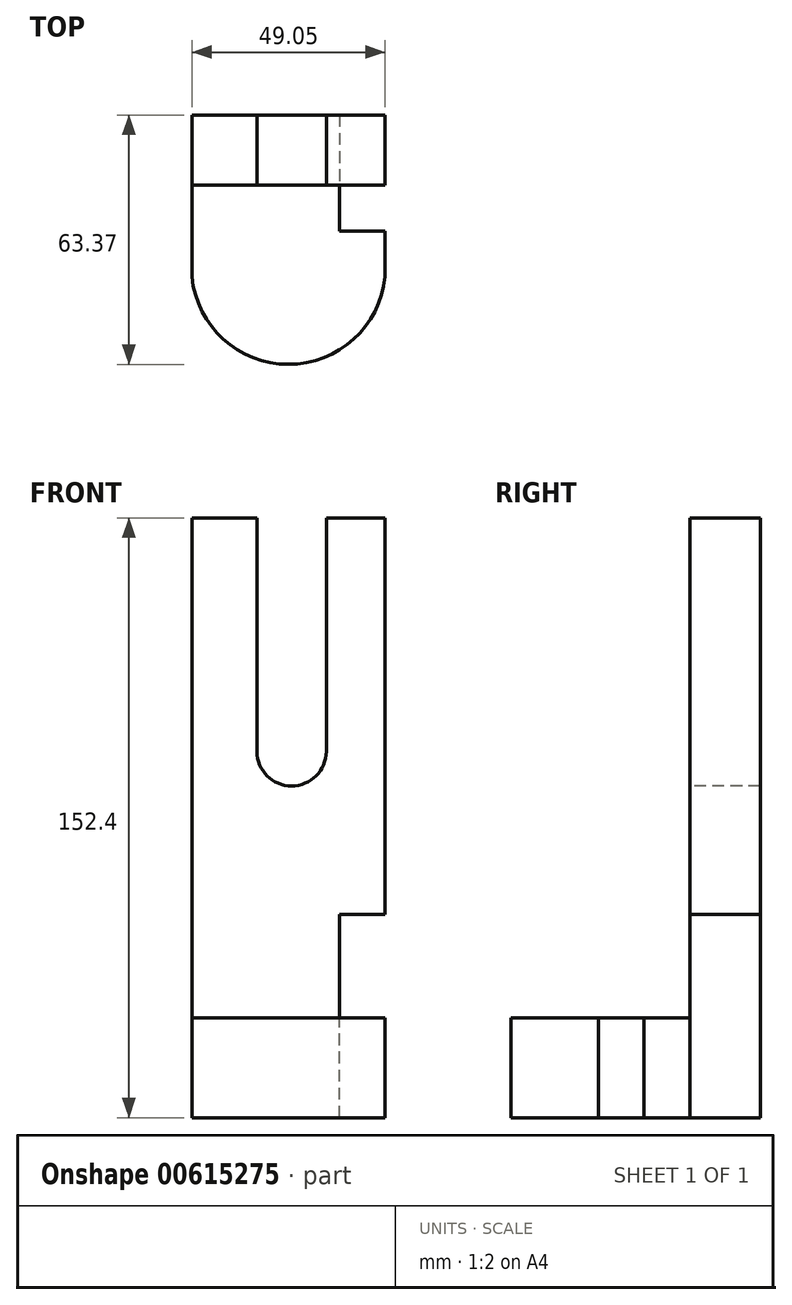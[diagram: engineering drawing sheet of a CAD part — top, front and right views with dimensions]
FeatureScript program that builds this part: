
annotation { "Feature Type Name" : "Feature", "Feature Type Description" : "" }
export const myFeature = defineFeature(function(context is Context, id is Id, definition is map)
    precondition{}
    {
        {
            var Q0;
            Q0=qCreatedBy(makeId("Top.planeOp"),FACE);
            var sketch = newSketch(context, id + "F0", { "sketchPlane" : qUnion([Q0])});
            skLineSegment(sketch, "E0.bottom", {"start": v(-76.32, -74.23) * mm, "end": v(-27.27, -74.23) * mm});
            skLineSegment(sketch, "E0.top", {"start": v(-76.32, -9.84) * mm, "end": v(-27.27, -9.84) * mm});
            skLineSegment(sketch, "E0.left", {"start": v(-76.32, -74.23) * mm, "end": v(-76.32, -9.84) * mm});
            skLineSegment(sketch, "E0.right", {"start": v(-27.27, -74.23) * mm, "end": v(-27.27, -9.84) * mm});
            skSolve(sketch);
        }
        {
            var Q0;
            Q0=makeQuery(id+"F0.imprint","IMPRINT",FACE,{"disambiguationData":[TD([[makeQuery(id+"F0.imprint","IMPRINT",EDGE,{"derivedFrom":sQuery(id+"F0.wireOp",EDGE,"E0.bottom")}),1.0]])]});
            extrude(context, id + "F1", {"entities" : qUnion([Q0]), "depth" : 25.4 * mm, "offsetDistance" : 25.4 * mm});
        }
        {
            var Q0;
            Q0=makeQuery(id+"F1.opExtrude","CAP_FACE",FACE,{"disambiguationData":[OSD([sQuery(id+"F0.wireOp",EDGE,"E0.bottom"),sQuery(id+"F0.wireOp",EDGE,"E0.top"),sQuery(id+"F0.wireOp",EDGE,"E0.left"),sQuery(id+"F0.wireOp",EDGE,"E0.right")])],"isStart":false});
            var sketch = newSketch(context, id + "F2", { "sketchPlane" : qUnion([Q0])});
            skLineSegment(sketch, "E1.bottom", {"start": v(-27.27, -9.84) * mm, "end": v(-76.32, -9.84) * mm});
            skLineSegment(sketch, "E1.top", {"start": v(-27.27, -27.72) * mm, "end": v(-76.32, -27.72) * mm});
            skLineSegment(sketch, "E1.left", {"start": v(-27.27, -9.84) * mm, "end": v(-27.27, -27.72) * mm});
            skLineSegment(sketch, "E1.right", {"start": v(-76.32, -9.84) * mm, "end": v(-76.32, -27.72) * mm});
            skSolve(sketch);
        }
        {
            var Q0;
            Q0=makeQuery(id+"F2.imprint","IMPRINT",FACE,{"disambiguationData":[TD([[makeQuery(id+"F2.imprint","IMPRINT",EDGE,{"derivedFrom":sQuery(id+"F2.wireOp",EDGE,"E1.bottom")}),-1.0]])]});
            extrude(context, id + "F3", {"entities" : qUnion([Q0]), "operationType" : NewBodyOperationType.ADD, "depth" : 127 * mm, "offsetDistance" : 25.4 * mm});
        }
        {
            var Q0;
            Q0=makeQuery(id+"F1.opExtrude","CAP_FACE",FACE,{"disambiguationData":[OSD([sQuery(id+"F0.wireOp",EDGE,"E0.bottom"),sQuery(id+"F0.wireOp",EDGE,"E0.top"),sQuery(id+"F0.wireOp",EDGE,"E0.left"),sQuery(id+"F0.wireOp",EDGE,"E0.right")])],"isStart":false});
            var sketch = newSketch(context, id + "F4", { "sketchPlane" : qUnion([Q0])});
            skArc(sketch, "E2", {"start": v(-76.32, -50.98) * mm, "mid": v(-51.8, -73.2) * mm, "end": v(-27.27, -50.98) * mm});
            skSolve(sketch);
        }
        {
            var Q0;
            {var subQ0=sQuery(id+"F4.wireOp",EDGE,"E2");Q0=makeQuery(id+"F4.imprint","IMPRINT",FACE,{"disambiguationData":[TD([[makeQuery(id+"F4.imprint","IMPRINT",EDGE,{"derivedFrom":subQ0}),-1.0]])]});}
            extrude(context, id + "F5", {"entities" : qUnion([Q0]), "operationType" : NewBodyOperationType.REMOVE, "oppositeDirection" : true, "depth" : 25.4 * mm, "offsetDistance" : 25.4 * mm});
        }
        {
            var Q0;
            Q0=makeQuery(id+"F1.opExtrude","CAP_FACE",FACE,{"disambiguationData":[OSD([sQuery(id+"F0.wireOp",EDGE,"E0.bottom"),sQuery(id+"F0.wireOp",EDGE,"E0.top"),sQuery(id+"F0.wireOp",EDGE,"E0.left"),sQuery(id+"F0.wireOp",EDGE,"E0.right")])],"isStart":false});
            var sketch = newSketch(context, id + "F6", { "sketchPlane" : qUnion([Q0])});
            skPoint(sketch, "E3.oppositeSnap0", {"position": v(-27.27, -39.35) * mm});
            skLineSegment(sketch, "E3.bottom", {"start": v(-27.27, -27.72) * mm, "end": v(-38.87, -27.72) * mm});
            skLineSegment(sketch, "E3.top", {"start": v(-27.27, -39.35) * mm, "end": v(-38.87, -39.35) * mm});
            skLineSegment(sketch, "E3.left", {"start": v(-27.27, -27.72) * mm, "end": v(-27.27, -39.35) * mm});
            skLineSegment(sketch, "E3.right", {"start": v(-38.87, -27.72) * mm, "end": v(-38.87, -39.35) * mm});
            skSolve(sketch);
        }
        {
            var Q0;
            Q0=makeQuery(id+"F6.imprint","IMPRINT",FACE,{"disambiguationData":[TD([[makeQuery(id+"F6.imprint","IMPRINT",EDGE,{"derivedFrom":sQuery(id+"F6.wireOp",EDGE,"E3.bottom")}),1.0]])]});
            extrude(context, id + "F7", {"entities" : qUnion([Q0]), "operationType" : NewBodyOperationType.REMOVE, "oppositeDirection" : true, "depth" : 25.4 * mm, "offsetDistance" : 25.4 * mm});
        }
        {
            var Q0;
            Q0=makeQuery(id+"F7.boolean.opBoolean","MERGE",FACE,{"derivedFrom":[makeQuery(id+"F3.opExtrude","SWEPT_FACE",FACE,{"disambiguationData":[OSD([sQuery(id+"F2.wireOp",EDGE,"E1.top")])]}),makeQuery(id+"F7.opExtrude","SWEPT_FACE",FACE,{"disambiguationData":[OSD([sQuery(id+"F6.wireOp",EDGE,"E3.bottom")])]})]});
            var sketch = newSketch(context, id + "F8", { "sketchPlane" : qUnion([Q0])});
            skLineSegment(sketch, "E4.bottom", {"start": v(-27.27, 0) * mm, "end": v(-38.8, 0) * mm});
            skLineSegment(sketch, "E4.top", {"start": v(-27.27, 51.68) * mm, "end": v(-38.8, 51.68) * mm});
            skLineSegment(sketch, "E4.left", {"start": v(-27.27, 0) * mm, "end": v(-27.27, 51.68) * mm});
            skLineSegment(sketch, "E4.right", {"start": v(-38.8, 0) * mm, "end": v(-38.8, 51.68) * mm});
            skSolve(sketch);
        }
        {
            var Q0;
            Q0=makeQuery(id+"F8.imprint","IMPRINT",FACE,{"disambiguationData":[TD([[makeQuery(id+"F8.imprint","IMPRINT",EDGE,{"derivedFrom":sQuery(id+"F8.wireOp",EDGE,"E4.bottom")}),-1.0]])]});
            extrude(context, id + "F9", {"entities" : qUnion([Q0]), "operationType" : NewBodyOperationType.REMOVE, "oppositeDirection" : true, "depth" : 25.4 * mm, "offsetDistance" : 25.4 * mm});
        }
        {
            var Q0;
            Q0=makeQuery(id+"F7.boolean.opBoolean","MERGE",FACE,{"derivedFrom":[makeQuery(id+"F3.opExtrude","SWEPT_FACE",FACE,{"disambiguationData":[OSD([sQuery(id+"F2.wireOp",EDGE,"E1.top")])]}),makeQuery(id+"F7.opExtrude","SWEPT_FACE",FACE,{"disambiguationData":[OSD([sQuery(id+"F6.wireOp",EDGE,"E3.bottom")])]})]});
            var sketch = newSketch(context, id + "F10", { "sketchPlane" : qUnion([Q0])});
            skLineSegment(sketch, "E5.bottom", {"start": v(-59.78, 152.4) * mm, "end": v(-42.16, 152.4) * mm});
            skLineSegment(sketch, "E5.left", {"start": v(-59.78, 152.4) * mm, "end": v(-59.78, 93.1) * mm});
            skLineSegment(sketch, "E5.right", {"start": v(-42.16, 152.4) * mm, "end": v(-42.16, 93.1) * mm});
            skArc(sketch, "E6", {"start": v(-59.78, 93.1) * mm, "mid": v(-50.97, 84.28) * mm, "end": v(-42.16, 93.1) * mm});
            skSolve(sketch);
        }
        {
            var Q0;
            Q0=makeQuery(id+"F10.imprint","IMPRINT",FACE,{"disambiguationData":[TD([[makeQuery(id+"F10.imprint","IMPRINT",EDGE,{"derivedFrom":sQuery(id+"F10.wireOp",EDGE,"E5.bottom")}),1.0]])]});
            extrude(context, id + "F11", {"entities" : qUnion([Q0]), "operationType" : NewBodyOperationType.REMOVE, "oppositeDirection" : true, "depth" : 25.4 * mm, "offsetDistance" : 25.4 * mm});
        }
    });
